# Revit family: PRD_AR_PprTwlDspnsrs_STRATOSElectronicPaperTowelDispenser_STRX630
name_source: partatom
category: Specialty Equipment
revit_build: Autodesk Revit 2018 (Build: 20190510_1515(x64)
units: mm (PartAtom-declared; Revit-internal decimal feet)

## family parameters
Cut with Voids When Loaded = No
Host = Face
OmniClass Number = 23.40.20.21.17
OmniClass Title = Paper Towel Dispensers, Disposal Units
Part Type = Normal
Room Calculation Point = No
Round Connector Dimension = Use Diameter
Shared = No

## types (1)
- STRX630
    AssetType = Fixed
    BIMObjectName = PRD_AR_PaperTowelDispensers_STRATOSElectronicPaperTowelDispenser_STRX630
    Category = Pr_40_70_22_62, Paper Towel Dispensers
    Default Elevation = 850 mm  [stored 2.78871 ft]
    Description = Touch free paper towel dispenser for wall mounting, stainless steel, surface satin finished, front with InoxPlus surface refinement for the reduction of finger marks and better cleaning characteristics (easy to clean), material thickness 1.5 mm, curved front cover, cylinder lock with KWC standard key, infrared sensor activity for non-touch operation, integrated tear-off edge, incl. 4 pcs. standard D 1.5 V batteries, maintenance free mechanic and easy paper roll change mechanism, for rolls with max. width 205 mm and max. diameter 200 mm, paper length adjustable to 200, 250 and 300 mm, includes stainless steel screws and dowels.
    DispenserMaterial = PRD_AR_StainlessSteel_SatinFinished
    DurationUnit = year
    Features = stainless steel, surface satin finished
    FillingQuantity = 1
    FillingQuantityUom = Rolls
    Finish = satin finished
    GrossWeight = 7.85 kg
    IfcExportAs = IfcFurnitureType
    IfcExportType = USERDEFINIED
    IntegralAccessories = incl. stainless steel screws and dowels
    IsBuiltIn = TRUE
    Lock = Key-lock
    MainColor = stainless steel
    Manufacturer = KWC Group AG
    ManufacturerName = KWC Group AG
    ManufacturerURL = www.kwc.com
    Material = stainless steel
    MaterialCode = 1.4301
    MaterialThickness = 1.50 mm
    MaximumDepthDiameterOfConsumable = 220.00 mm
    MaximumDepthOfConsumable = 205.00 mm
    Model = STRX630
    ModelNumber = 2000057390
    ModelReference = STRX630
    NBSDescription = Paper towel dispensers
    NBSReference = 45-35-72/344
    Name = Electronic Paper Towel Dispenser STRX630
    NetWeight = 6.85 kg
    NominalDepth = 234 mm  [stored 0.767717 ft]
    NominalHeight = 383 mm  [stored 1.25656 ft]
    NominalWidth = 300 mm  [stored 0.984252 ft]
    NumberOfBatteries = 4
    ProductInformation = https://pim.kwc.com
    Size = 300 x 383 x 234 mm
    Style = dispenser
    SurfaceTreatment = InoxPlus (anti fingerprint)
    TypeOfBatteries = D Mono battery 1.5 V
    TypeOfConsumable = Paper roll
    TypeOfFixing = Screw
    TypeOfMounting = Wall mounting
    TypeOfOperation = Sensor operation
    URL = www.kwc.com
    Uniclass2015Code = Pr_40_70_22_62
    Uniclass2015Title = Paper towel dispensers
    Uniclass2015Version = Products v1.10
    Version = 1
    WarrantyDurationUnit = year

note: [stored X ft] marks values corroborated as IEEE doubles in the binary element streams (Revit-internal decimal feet)

## geometry (parser evidence)
native form markers: Sweep x4
no freeform markers — native parametric forms only
